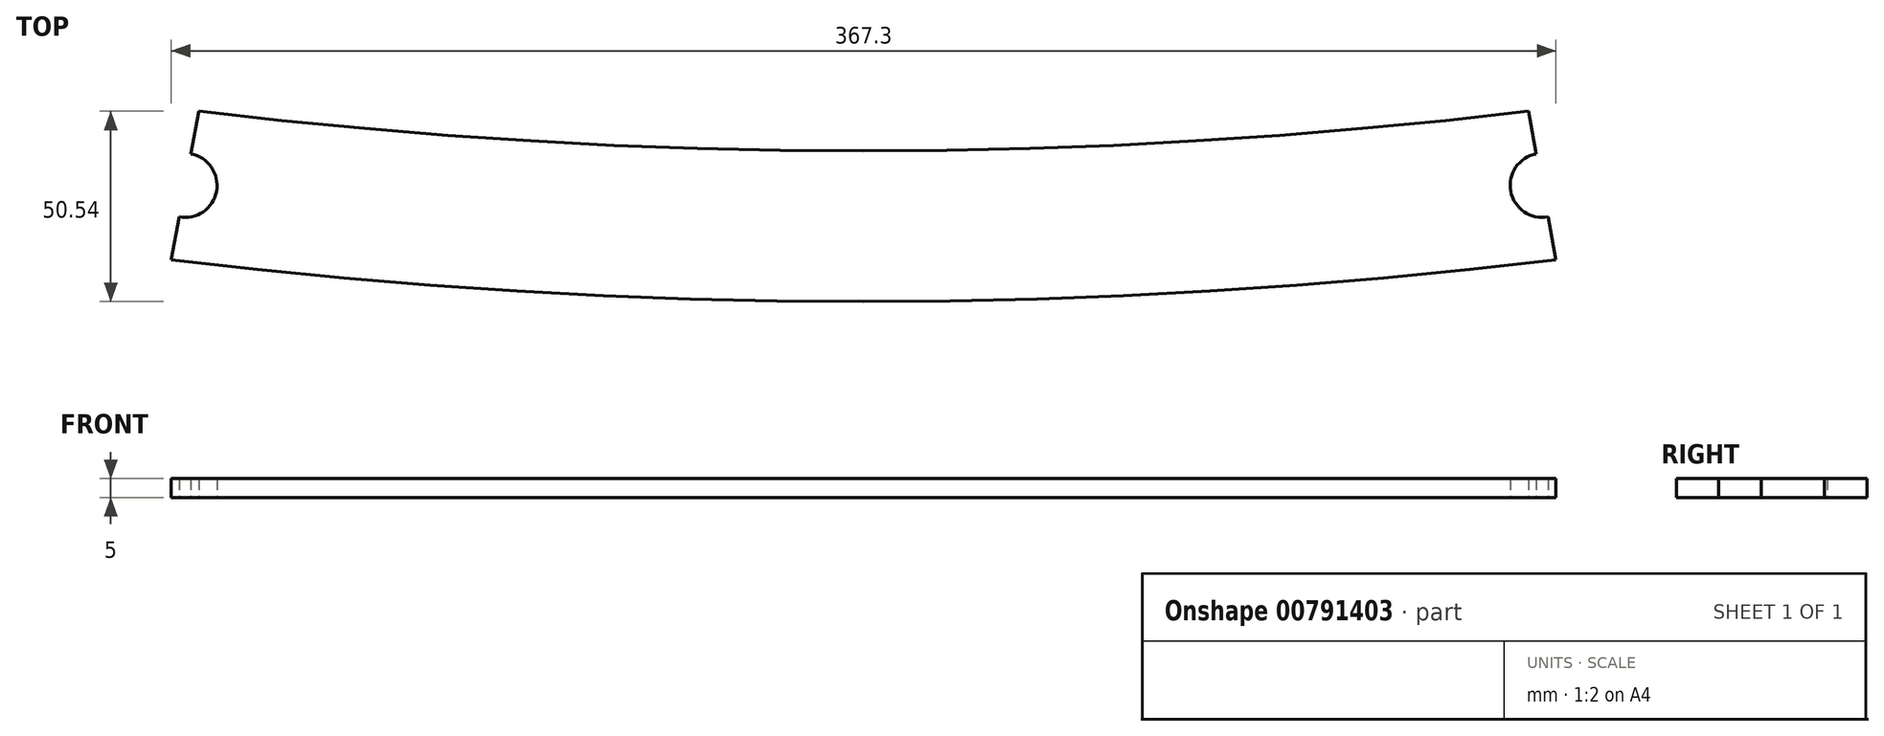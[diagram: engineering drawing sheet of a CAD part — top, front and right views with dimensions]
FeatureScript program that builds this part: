
annotation { "Feature Type Name" : "Feature", "Feature Type Description" : "" }
export const myFeature = defineFeature(function(context is Context, id is Id, definition is map)
    precondition{}
    {
        {
            var Q0;
            Q0=qCreatedBy(makeId("Top.planeOp"),FACE);
            var sketch = newSketch(context, id + "F0", { "sketchPlane" : qUnion([Q0])});
            skArc(sketch, "E0", {"start": v(-180, -19.7) * mm, "mid": v(0, -30.54) * mm, "end": v(180, -19.7) * mm, "construction": true});
            skArc(sketch, "E1", {"start": v(-176.35, 0) * mm, "mid": v(0, -10.54) * mm, "end": v(176.35, 0) * mm});
            skArc(sketch, "E2", {"start": v(-183.65, -39.4) * mm, "mid": v(0, -50.54) * mm, "end": v(183.65, -39.4) * mm});
            skLineSegment(sketch, "E3", {"start": v(176.35, 0) * mm, "end": v(178.45, -11.35) * mm});
            skLineSegment(sketch, "E4", {"start": v(-176.35, 0) * mm, "end": v(-178.45, -11.35) * mm});
            skArc(sketch, "E5", {"start": v(-181.55, -28.06) * mm, "mid": v(-171.64, -21.25) * mm, "end": v(-178.45, -11.35) * mm});
            skLineSegment(sketch, "E6.trimOffspring", {"start": v(-181.55, -28.06) * mm, "end": v(-183.65, -39.4) * mm});
            skArc(sketch, "E7.MirrorCS", {"start": v(181.55, -28.06) * mm, "mid": v(171.64, -21.25) * mm, "end": v(178.45, -11.35) * mm});
            skLineSegment(sketch, "E8.trimOffspring", {"start": v(181.55, -28.06) * mm, "end": v(183.65, -39.4) * mm});
            skSolve(sketch);
        }
        {
            var Q0;
            Q0 = qSketchRegion(id + "F0", true);
            extrude(context, id + "F1", {"entities" : qUnion([Q0]), "depth" : 5 * mm, "offsetDistance" : 25 * mm});
        }
    });
